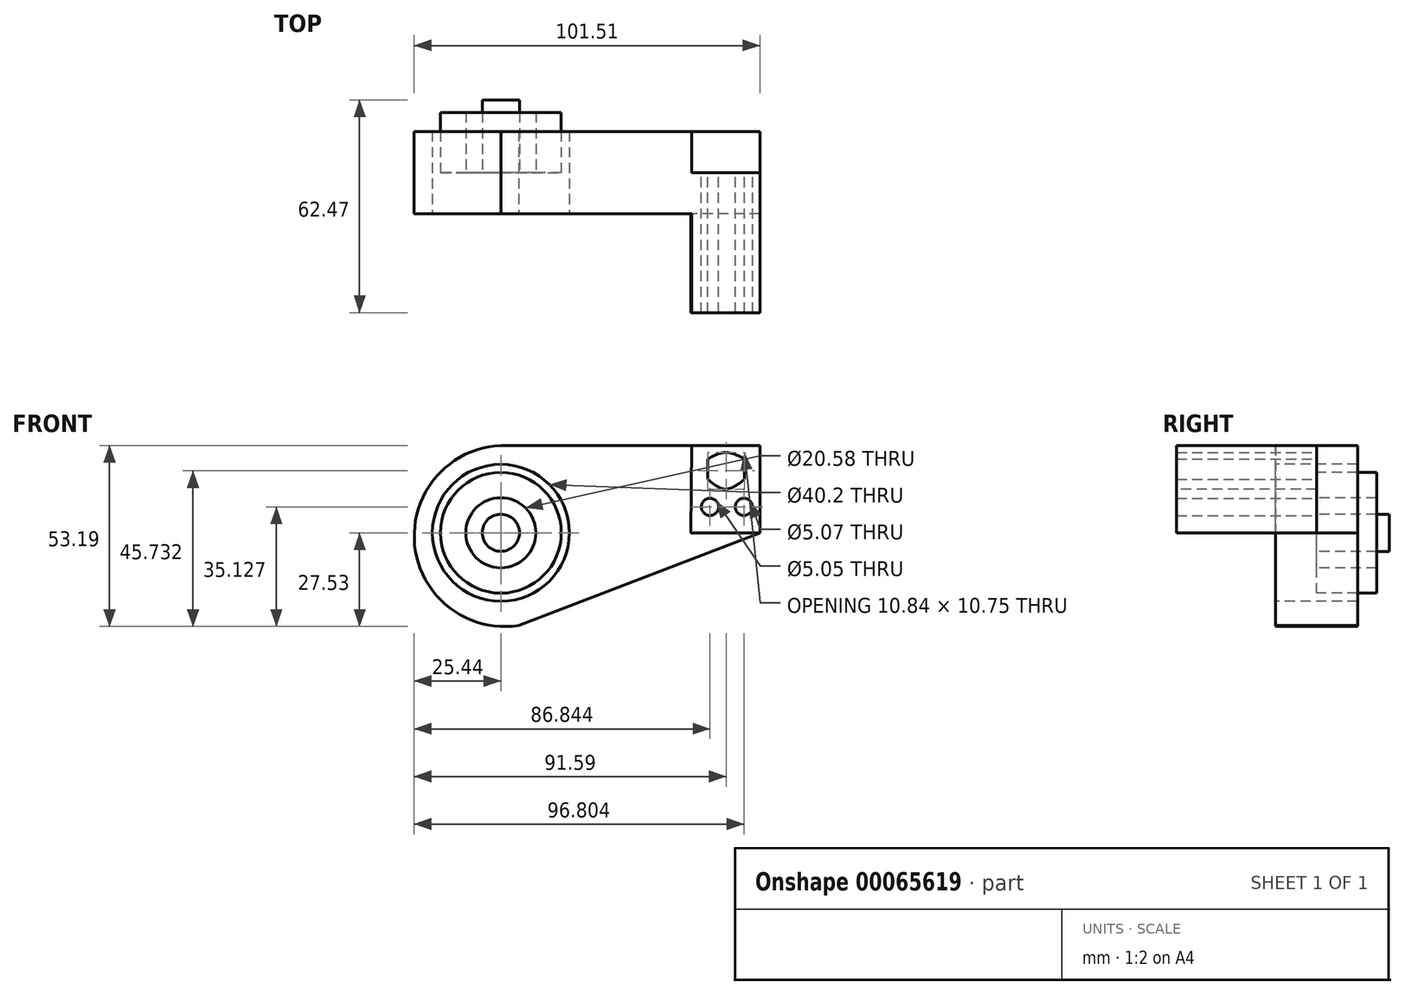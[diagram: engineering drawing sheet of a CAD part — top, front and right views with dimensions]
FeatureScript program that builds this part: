
annotation { "Feature Type Name" : "Feature", "Feature Type Description" : "" }
export const myFeature = defineFeature(function(context is Context, id is Id, definition is map)
    precondition{}
    {
        {
            var Q0;
            Q0=qCreatedBy(makeId("Front.planeOp"),FACE);
            var sketch = newSketch(context, id + "F0", { "sketchPlane" : qUnion([Q0])});
            skCircle(sketch, "E0", {"center": v(0, 0) * mm, "radius": 5.46 * mm});
            skCircle(sketch, "E1", {"center": v(0, 0) * mm, "radius": 20.1 * mm});
            skArc(sketch, "E2", {"start": v(0, 25.66) * mm, "mid": v(-25.3, -3.56) * mm, "end": v(5.27, -27.22) * mm});
            skLineSegment(sketch, "E3", {"start": v(0, 25.66) * mm, "end": v(56.07, 25.66) * mm});
            skLineSegment(sketch, "E4", {"start": v(56.07, 25.66) * mm, "end": v(76.07, 25.66) * mm});
            skLineSegment(sketch, "E5", {"start": v(76.07, 25.66) * mm, "end": v(76.07, 0) * mm});
            skLineSegment(sketch, "E6", {"start": v(76.07, 0) * mm, "end": v(55.84, 0) * mm});
            skLineSegment(sketch, "E7", {"start": v(55.84, 0) * mm, "end": v(56.07, 25.66) * mm});
            skCircle(sketch, "E8", {"center": v(61.4, 7.6) * mm, "radius": 2.52 * mm});
            skCircle(sketch, "E9", {"center": v(71.36, 7.6) * mm, "radius": 2.53 * mm});
            skPoint(sketch, "E10", {"position": v(66.07, 25.66) * mm});
            skLineSegment(sketch, "E11", {"start": v(60.78, 21.7) * mm, "end": v(60.73, 15.7) * mm});
            skLineSegment(sketch, "E12", {"start": v(71.57, 21.7) * mm, "end": v(71.57, 15.7) * mm});
            skFitSpline(sketch, "E13", {"points": [v(60.78, 21.7) * mm, v(65.97, 23.58) * mm, v(71.57, 21.7) * mm], "startDerivative": vector(10.44, 5.64) * mm, "endDerivative": vector(11.13, -5.57) * mm});
            skPoint(sketch, "E14.1.internal.snap0", {"position": v(55.96, 12.83) * mm});
            skFitSpline(sketch, "E14", {"points": [v(60.73, 15.7) * mm, v(65.97, 12.83) * mm, v(71.57, 15.7) * mm], "startDerivative": vector(10.51, -8.63) * mm, "endDerivative": vector(11.17, 8.56) * mm});
            skLineSegment(sketch, "E15", {"start": v(55.94, 11.33) * mm, "end": v(76.07, 11.15) * mm});
            skLineSegment(sketch, "E16", {"start": v(5.27, -27.22) * mm, "end": v(76.07, 0) * mm});
            skCircle(sketch, "E17", {"center": v(0, 0) * mm, "radius": 10.29 * mm});
            skCircle(sketch, "E18", {"center": v(0, 0) * mm, "radius": 17.74 * mm});
            skSolve(sketch);
        }
        {
            var Q0;
            Q0=makeQuery(id+"F0.imprint","IMPRINT",FACE,{"disambiguationData":[TD([[makeQuery(id+"F0.imprint","IMPRINT",EDGE,{"derivedFrom":sQuery(id+"F0.wireOp",EDGE,"E0")}),1.0]])]});
            extrude(context, id + "F1", {"entities" : qUnion([Q0]), "oppositeDirection" : true, "depth" : 21.33 * mm});
        }
        {
            var Q0;
            Q0=makeQuery(id+"F0.imprint","IMPRINT",FACE,{"disambiguationData":[TD([[makeQuery(id+"F0.imprint","IMPRINT",EDGE,{"derivedFrom":sQuery(id+"F0.wireOp",EDGE,"E17")}),-1.0]])]});
            extrude(context, id + "F2", {"entities" : qUnion([Q0]), "oppositeDirection" : true, "depth" : 17.63 * mm});
        }
        {
            var Q0;
            Q0=makeQuery(id+"F0.imprint","IMPRINT",FACE,{"disambiguationData":[TD([[makeQuery(id+"F0.imprint","IMPRINT",EDGE,{"derivedFrom":sQuery(id+"F0.wireOp",EDGE,"E1")}),-1.0]])]});
            extrude(context, id + "F3", {"entities" : qUnion([Q0]), "endBound" : BoundingType.SYMMETRIC, "oppositeDirection" : true, "depth" : 24.14 * mm});
        }
        {
            var Q0;
            {var subQ1=sQuery(id+"F0.wireOp",EDGE,"E4");Q0=makeQuery(id+"F0.imprint","IMPRINT",FACE,{"disambiguationData":[TD([[makeQuery(id+"F0.imprint","IMPRINT",EDGE,{"derivedFrom":subQ1}),-1.0]])]});}
            var Q1;
            {var subQ1=sQuery(id+"F0.wireOp",EDGE,"E6");Q1=makeQuery(id+"F0.imprint","IMPRINT",FACE,{"disambiguationData":[TD([[makeQuery(id+"F0.imprint","IMPRINT",EDGE,{"derivedFrom":subQ1}),-1.0]])]});}
            extrude(context, id + "F4", {"entities" : qUnion([Q0, Q1]), "operationType" : NewBodyOperationType.ADD, "depth" : 41.14 * mm});
        }
    });
